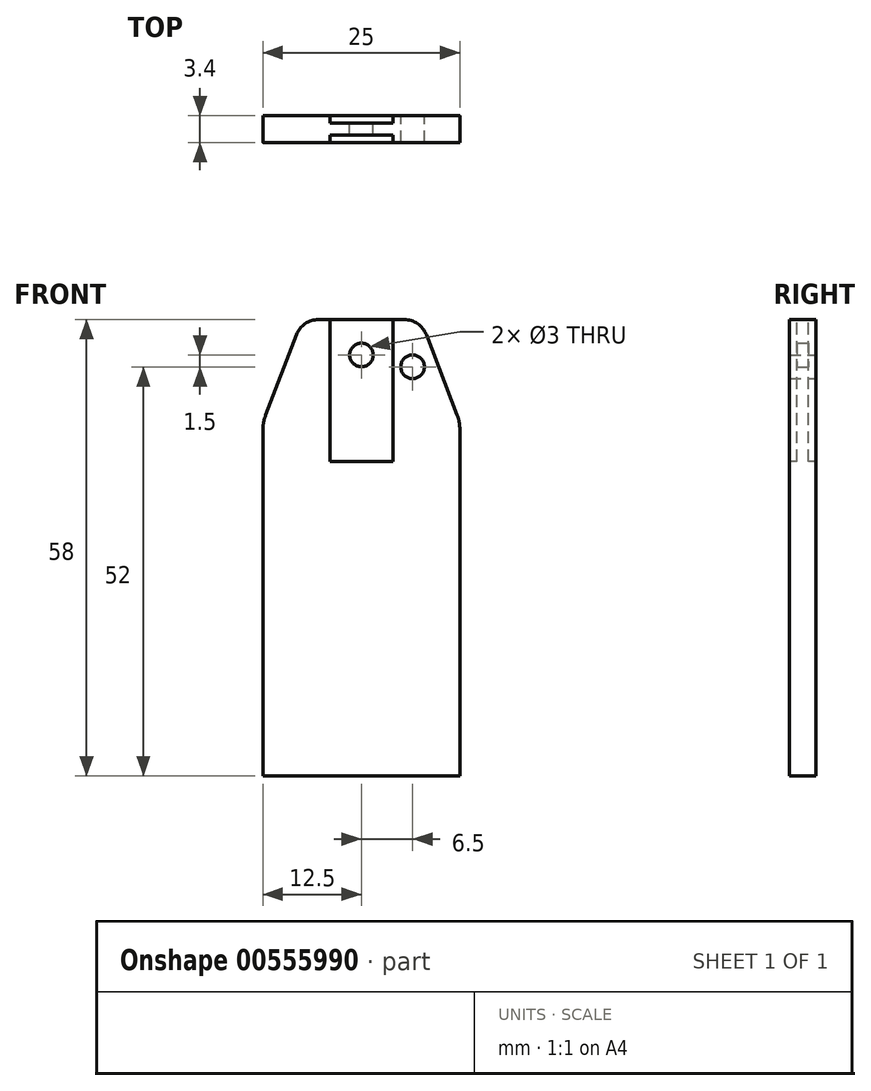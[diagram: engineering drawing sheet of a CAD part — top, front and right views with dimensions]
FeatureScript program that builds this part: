
annotation { "Feature Type Name" : "Feature", "Feature Type Description" : "" }
export const myFeature = defineFeature(function(context is Context, id is Id, definition is map)
    precondition{}
    {
        {
            assignVariable(context, id + "F0", {"name" : "thick", "anyValue" : 3.4});
        }
        {
            var Q0;
            Q0=qCreatedBy(makeId("Front.planeOp"),FACE);
            var sketch = newSketch(context, id + "F1", { "sketchPlane" : qUnion([Q0])});
            skLineSegment(sketch, "E0.bottom", {"start": v(12.5, 22.5) * mm, "end": v(-12.5, 22.5) * mm});
            skLineSegment(sketch, "E0.top", {"start": v(12.5, -22.5) * mm, "end": v(-12.5, -22.5) * mm});
            skLineSegment(sketch, "E0.left", {"start": v(12.5, 22.5) * mm, "end": v(12.5, -22.5) * mm});
            skLineSegment(sketch, "E0.right", {"start": v(-12.5, 22.5) * mm, "end": v(-12.5, -22.5) * mm});
            skPoint(sketch, "E0.middle", {"position": v(0, 0) * mm});
            skLineSegment(sketch, "E1.bottom", {"start": v(7.5, 35.5) * mm, "end": v(-7.5, 35.5) * mm});
            skLineSegment(sketch, "E1.top", {"start": v(7.5, 9.5) * mm, "end": v(-7.5, 9.5) * mm});
            skLineSegment(sketch, "E1.left", {"start": v(7.5, 35.5) * mm, "end": v(7.5, 9.5) * mm});
            skLineSegment(sketch, "E1.right", {"start": v(-7.5, 35.5) * mm, "end": v(-7.5, 9.5) * mm});
            skPoint(sketch, "E1.middle", {"position": v(0, 22.5) * mm});
            skLineSegment(sketch, "E2", {"start": v(-7.5, 35.5) * mm, "end": v(-12.5, 22.5) * mm});
            skLineSegment(sketch, "E3", {"start": v(7.5, 35.5) * mm, "end": v(12.5, 22.5) * mm});
            skCircle(sketch, "E4", {"center": v(0, 31) * mm, "radius": 1.5 * mm});
            skCircle(sketch, "E5", {"center": v(6.5, 29.5) * mm, "radius": 1.5 * mm});
            skSolve(sketch);
        }
        {
            var Q0;
            Q0=qSketchRegion(id+"F1",true);
            var Q1;
            {var subQ5=sQuery(id+"F1.wireOp",EDGE,"E1.top");Q1=makeQuery(id+"F1.imprint","IMPRINT",FACE,{"disambiguationData":[TD([[makeQuery(id+"F1.imprint","IMPRINT",EDGE,{"derivedFrom":subQ5}),-1.0]])]});}
            extrude(context, id + "F2", {"entities" : qUnion([Q0, Q1]), "depth" : (getVariable(context, 'thick')) * mm, "offsetDistance" : 25 * mm});
        }
        {
            var Q0;
            Q0=makeQuery(id+"F2.opExtrude","SWEPT_FACE",FACE,{"disambiguationData":[OSD([sQuery(id+"F1.wireOp",EDGE,"E1.bottom")])]});
            var sketch = newSketch(context, id + "F3", { "sketchPlane" : qUnion([Q0])});
            skLineSegment(sketch, "E6.bottom", {"start": v(4, 0) * mm, "end": v(-4, 0) * mm});
            skLineSegment(sketch, "E6.top", {"start": v(4, -3.4) * mm, "end": v(-4, -3.4) * mm});
            skLineSegment(sketch, "E6.left", {"start": v(4, 0) * mm, "end": v(4, -3.4) * mm});
            skLineSegment(sketch, "E6.right", {"start": v(-4, 0) * mm, "end": v(-4, -3.4) * mm});
            skPoint(sketch, "E6.middle.positionSnap0", {"position": v(0, 0) * mm});
            skPoint(sketch, "E6.centerSnap0", {"position": v(0, 0) * mm});
            skPoint(sketch, "E7.middle", {"position": v(4, -3.4) * mm});
            skLineSegment(sketch, "E8", {"start": v(-4, -1.7) * mm, "end": v(4, -1.7) * mm});
            skLineSegment(sketch, "E9.bottom", {"start": v(4, -0.95) * mm, "end": v(-4, -0.95) * mm});
            skLineSegment(sketch, "E9.top", {"start": v(4, -2.45) * mm, "end": v(-4, -2.45) * mm});
            skLineSegment(sketch, "E9.left", {"start": v(4, -0.95) * mm, "end": v(4, -2.45) * mm});
            skLineSegment(sketch, "E9.right", {"start": v(-4, -0.95) * mm, "end": v(-4, -2.45) * mm});
            skPoint(sketch, "E9.middle", {"position": v(0, -1.7) * mm});
            skSolve(sketch);
        }
        {
            var Q0;
            {var subQ0=sQuery(id+"F3.wireOp",EDGE,"E6.bottom");Q0=makeQuery(id+"F3.imprint","IMPRINT",FACE,{"disambiguationData":[TD([[makeQuery(id+"F3.imprint","IMPRINT",EDGE,{"derivedFrom":subQ0}),1.0]])]});}
            extrude(context, id + "F4", {"entities" : qUnion([Q0]), "operationType" : NewBodyOperationType.REMOVE, "oppositeDirection" : true, "depth" : 18 * mm, "offsetDistance" : 25 * mm});
        }
        {
            var Q0;
            {var subQ0=sQuery(id+"F3.wireOp",EDGE,"E6.top");Q0=makeQuery(id+"F3.imprint","IMPRINT",FACE,{"disambiguationData":[TD([[makeQuery(id+"F3.imprint","IMPRINT",EDGE,{"derivedFrom":subQ0}),-1.0]])]});}
            extrude(context, id + "F5", {"entities" : qUnion([Q0]), "operationType" : NewBodyOperationType.REMOVE, "oppositeDirection" : true, "depth" : 18 * mm, "offsetDistance" : 25 * mm});
        }
        {
            var Q0;
            Q0=makeQuery(id+"F2.opExtrude","SWEPT_EDGE",EDGE,{"disambiguationData":[OSD([sQuery(id+"F1.wireOp",EDGE,"E1.bottom"),sQuery(id+"F1.wireOp",EDGE,"E1.right"),sQuery(id+"F1.wireOp",EDGE,"E2")])]});
            fillet(context, id + "F6", {"entities" : qUnion([Q0]), "radius" : 3 * mm, "tangentPropagation" : true, "allowEdgeOverflow" : false});
        }
        {
            var Q0;
            Q0=makeQuery(id+"F2.opExtrude","SWEPT_EDGE",EDGE,{"disambiguationData":[OSD([sQuery(id+"F1.wireOp",EDGE,"E1.bottom"),sQuery(id+"F1.wireOp",EDGE,"E1.left"),sQuery(id+"F1.wireOp",EDGE,"E3")])]});
            fillet(context, id + "F7", {"entities" : qUnion([Q0]), "radius" : 3 * mm, "tangentPropagation" : true, "allowEdgeOverflow" : false});
        }
        {
            var Q0;
            Q0=makeQuery(id+"F2.opExtrude","SWEPT_EDGE",EDGE,{"disambiguationData":[OSD([sQuery(id+"F1.wireOp",EDGE,"E0.bottom"),sQuery(id+"F1.wireOp",EDGE,"E0.left"),sQuery(id+"F1.wireOp",EDGE,"E3")])]});
            fillet(context, id + "F8", {"entities" : qUnion([Q0]), "radius" : 5 * mm, "tangentPropagation" : true, "allowEdgeOverflow" : false});
        }
        {
            var Q0;
            Q0=makeQuery(id+"F2.opExtrude","SWEPT_EDGE",EDGE,{"disambiguationData":[OSD([sQuery(id+"F1.wireOp",EDGE,"E0.bottom"),sQuery(id+"F1.wireOp",EDGE,"E0.right"),sQuery(id+"F1.wireOp",EDGE,"E2")])]});
            fillet(context, id + "F9", {"entities" : qUnion([Q0]), "radius" : 5 * mm, "tangentPropagation" : true, "allowEdgeOverflow" : false});
        }
    });
